FCSTD DOCUMENT  (FreeCAD 0.14R3702 (Git))
Label: Everext
License: CC-BY 3.0
LicenseURL: http://creativecommons.org/licenses/by/3.0/
objects: Mesh::Feature×51, Part::Cylinder×36, Part::Cut×32, Part::MultiFuse×20, Part::Feature×20, PartDesign::Chamfer×20, Part::FeaturePython×16, App::DocumentObjectGroup×16, Part::Box×15, PartDesign::Pad×12, Sketcher::SketchObject×9, PartDesign::Pocket×7, Part::Sweep×5, Part::Mirroring×3, PartDesign::Revolution×2, Part::Chamfer×2, Part::Helix×1
note: 221 computed .brp shape members not serialized (recipe doc carries the construction recipe); baked Part::Feature solids carry a one-line shape summary decoded from their .brp

FEATURE [PartDesign::Pad] Pad  label="Pata001"
  Length = 335
  Length2 = 100
  Placement = pos=(-110,-110,-167.5) rot=(0,0,1;0rad)
  Type = 0
FEATURE [PartDesign::Pad] Pad001  label="Pata002"
  Length = 335
  Length2 = 100
  Placement = pos=(110,-110,-167.5) rot=(0,0,1;0rad)
  Type = 0
FEATURE [PartDesign::Pad] Pad002  label="Pata003"
  Length = 335
  Length2 = 100
  Placement = pos=(-110,110,-167.5) rot=(0,0,1;0rad)
  Type = 0
FEATURE [PartDesign::Pad] Pad003  label="Pata004"
  Length = 335
  Length2 = 100
  Placement = pos=(110,110,-167.5) rot=(0,0,1;0rad)
  Type = 0
FEATURE [PartDesign::Pad] Pad004  label="Trab001"
  Length = 200
  Length2 = 100
  Placement = pos=(-100,-110,-119) rot=(0,1,0;1.5708rad)
  Type = 0
FEATURE [PartDesign::Pad] Pad005  label="Trab002"
  Length = 200
  Length2 = 100
  Placement = pos=(-110,-100,-119) rot=(0.57735,-0.57735,-0.57735;4.18879rad)
  Type = 0
FEATURE [PartDesign::Pad] Pad006  label="Trab003"
  Length = 200
  Length2 = 100
  Placement = pos=(110,-100,-119) rot=(0.57735,-0.57735,-0.57735;4.18879rad)
  Type = 0
FEATURE [PartDesign::Pad] Pad007  label="Trab004"
  Length = 200
  Length2 = 100
  Placement = pos=(-100,110,-119) rot=(0,1,0;1.5708rad)
  Type = 0
FEATURE [PartDesign::Pad] Pad008  label="Trab005"
  Length = 200
  Length2 = 100
  Placement = pos=(-100,-110,157.5) rot=(0,1,0;1.5708rad)
  Type = 0
FEATURE [PartDesign::Pad] Pad009  label="Trab006"
  Length = 200
  Length2 = 100
  Placement = pos=(-110,-100,157.5) rot=(0.57735,-0.57735,-0.57735;4.18879rad)
  Type = 0
FEATURE [PartDesign::Pad] Pad010  label="Trab007"
  Length = 200
  Length2 = 100
  Placement = pos=(110,-100,157.5) rot=(0.57735,-0.57735,-0.57735;4.18879rad)
  Type = 0
FEATURE [PartDesign::Pad] Pad011  label="Trab008"
  Length = 200
  Length2 = 100
  Placement = pos=(-100,110,157.5) rot=(0,1,0;1.5708rad)
  Type = 0
FEATURE [PartDesign::Pocket] Pocket006
  Length = 3
  Type = 0
FEATURE [Part::FeaturePython] refine  label="motor"  # WARN: FeaturePython — macro-defined, semantics opaque (R4)
  Base = -> Pocket006
  Placement = pos=(68,100,60.5) rot=(0,0,1;0rad)
FEATURE [Part::Cylinder] Cylinder008  label="BarraIz"
  Angle = 360
  Height = 190
  Placement = pos=(-110,-99,117.5) rot=(-0.57735,0.57735,0.57735;2.0944rad)
  Radius = 4
FEATURE [Part::FeaturePython] refine001  label="motor001"  # WARN: FeaturePython — macro-defined, semantics opaque (R4)
  Base = -> Pocket006
  Placement = pos=(-68,100,60.5) rot=(0,0,1;0rad)
FEATURE [Part::Cylinder] Cylinder009  label="barraM8Xmotor"
  Angle = 360
  Height = 190
  Placement = pos=(95,-12,105.5) rot=(0.707107,0,-0.707107;3.14159rad)
  Radius = 4
FEATURE [Part::Cylinder] Cylinder010  label="BarraDer"
  Angle = 360
  Height = 190
  Placement = pos=(110,-99,117.5) rot=(-0.57735,0.57735,0.57735;2.0944rad)
  Radius = 4
FEATURE [App::DocumentObjectGroup] Grupo006  label="barras"
  Group = -> [Cylinder008,Cylinder010]
FEATURE [Part::Cylinder] Cylinder011  label="barraM8X"
  Angle = 360
  Height = 190
  Placement = pos=(95,-12,129.5) rot=(0.707107,0,-0.707107;3.14159rad)
  Radius = 4
FEATURE [Part::Cylinder] Cylinder014  label="barraM8008"
  Angle = 360
  Height = 235
  Placement = pos=(-35,79,-116.5) rot=(0,0,1;0rad)
  Radius = 4
FEATURE [Part::Cylinder] Cylinder015  label="barraM8009"
  Angle = 360
  Height = 235
  Placement = pos=(35,79,-116.5) rot=(0,0,1;0rad)
  Radius = 4
FEATURE [Mesh::Feature] Z_lift
  Placement = pos=(107,253.5,219.1) rot=(0,0,1;1.5708rad)
FEATURE [Mesh::Feature] printable_lm8uu_v007  label="printable-lm8uu-v004"
  Placement = pos=(33.4,85.2,-3.9) rot=(0,0,1;0rad)
FEATURE [Mesh::Feature] printable_lm8uu_v008  label="printable-lm8uu-v005"
  Placement = pos=(-36.6,85.2,-3.9) rot=(0,0,1;0rad)
FEATURE [Part::Box] Box  label="tablelisa"
  Height = 3
  Length = 120
  Placement = pos=(53,45,161) rot=(0,0,1;0rad)
  Width = 120
FEATURE [Part::FeaturePython] refine002  label="motor002"  # WARN: FeaturePython — macro-defined, semantics opaque (R4)
  Placement = pos=(0,79,-168) rot=(0,0,1;0rad)
FEATURE [Part::Cylinder] Cylinder016  label="Cilindro008"
  Angle = 360
  Height = 10
  Placement = pos=(79.5,114.1,158) rot=(0,0,1;0rad)
  Radius = 2.6
FEATURE [Part::Cylinder] Cylinder017  label="Cilindro009"
  Angle = 360
  Height = 10
  Placement = pos=(144.5,114.1,158) rot=(0,0,1;0rad)
  Radius = 2.6
FEATURE [Part::Cylinder] Cylinder018  label="Cilindro010"
  Angle = 360
  Height = 10
  Placement = pos=(144.5,152.1,158) rot=(0,0,1;0rad)
  Radius = 2.6
FEATURE [Part::Cylinder] Cylinder019  label="Cilindro011"
  Angle = 360
  Height = 10
  Placement = pos=(79.5,152.1,158) rot=(0,0,1;0rad)
  Radius = 2.6
FEATURE [Part::Cut] Cut008
  Base = -> Box
  Tool = -> Cylinder016
FEATURE [Part::Cut] Cut009
  Base = -> Cut008
  Tool = -> Cylinder017
FEATURE [Part::Cut] Cut010
  Base = -> Cut009
  Tool = -> Cylinder019
FEATURE [Part::Cut] Cut011  label="mesainf01"
  Base = -> Cut010
  Tool = -> Cylinder018
FEATURE [Part::Box] Box001  label="tablelisa001"
  Height = 3
  Length = 120
  Placement = pos=(53,45,174) rot=(0,0,1;0rad)
  Width = 120
FEATURE [Sketcher::SketchObject] Sketch
  Placement = pos=(53,45,177) rot=(0,0,1;0rad)
  Support = -> Box001 [Face6]
  sketch-geometry (3):
    g0: Circle CenterX=5 CenterY=5 CenterZ=0 NormalX=0 NormalY=0 NormalZ=1 Radius=1.5
    g1: Circle CenterX=115 CenterY=5 CenterZ=0 NormalX=0 NormalY=0 NormalZ=1 Radius=1.5
    g2: Circle CenterX=60 CenterY=105 CenterZ=0 NormalX=0 NormalY=0 NormalZ=1 Radius=1.5
  constraints (9):
    c: Equal(g2,g1)
    c: Equal(g1,g0)
    c: Radius(g0) = 1.5
    c: DistanceY(g-1,g0) = 5
    c: DistanceX(g-1,g0) = 5
    c: DistanceY(g-1,g1) = 5
    c: DistanceX(g-1,g1) = 115
    c: DistanceY(g-1,g2) = 105
    c: DistanceX(g-1,g2) = 60
FEATURE [PartDesign::Pocket] Pocket  label="mesasup"
  Length = 5
  Placement = pos=(53,45,174) rot=(0,0,1;0rad)
  Sketch = -> Sketch
  Type = 1
FEATURE [Sketcher::SketchObject] Sketch001
  ExternalGeometry = -> [Cut011]
  Placement = pos=(0,0,164) rot=(0,0,1;0rad)
  Support = -> Cut011 [Face3]
  sketch-geometry (3):
    g0: Circle CenterX=58 CenterY=50 CenterZ=0 NormalX=0 NormalY=0 NormalZ=1 Radius=1.5
    g1: Circle CenterX=168 CenterY=50 CenterZ=0 NormalX=0 NormalY=0 NormalZ=1 Radius=1.5
    g2: Circle CenterX=113 CenterY=150 CenterZ=0 NormalX=0 NormalY=0 NormalZ=1 Radius=1.5
  constraints (9):
    c: Equal(g2,g1)
    c: Equal(g1,g0)
    c: Radius(g1) = 1.5
    c: DistanceX(g0,g-4) = -5
    c: DistanceY(g0,g-4) = -5
    c: DistanceX(g1,g-4) = 5
    c: DistanceY(g1,g-4) = -5
    c: DistanceX(g2,g-3) = -60
    c: DistanceY(g2,g-3) = 15
FEATURE [PartDesign::Pocket] Pocket007  label="mesainf"
  Length = 5
  Sketch = -> Sketch001
  Type = 1
FEATURE [Part::MultiFuse] Fusion004
FEATURE [Part::Helix] Helix  label="Muelletrazo"
  Angle = 0
  Height = 9.4
  LocalCoord = 0
  Pitch = 1
  Placement = pos=(0,0,8) rot=(0,0,1;0rad)
  Radius = 2.5
  Style = 1
FEATURE [Part::Sweep] Sweep
  Frenet = true
  Solid = true
  Spine = -> Helix [Edge1]
  Transition = 1
FEATURE [Part::MultiFuse] Fusion005  label="tonillocama"
  Placement = pos=(-54,-59,-11) rot=(0,0,1;0rad)
  Shapes = -> [Fusion004,Sweep]
FEATURE [Part::Sweep] Sweep001
  Frenet = true
  Solid = true
  Spine = -> Helix [Edge1]
  Transition = 1
FEATURE [Part::MultiFuse] Fusion006
FEATURE [Part::MultiFuse] Fusion007  label="tonillocama001"
  Placement = pos=(56,-59,-11) rot=(0,0,1;0rad)
  Shapes = -> [Fusion006,Sweep001]
FEATURE [Part::Cut] Cut012
FEATURE [Part::FeaturePython] Array  # Draft array (typed FeaturePython)
  Angle = 360
  ArrayType = 1
  Axis = (0,0,1)
  Center = (0,0,0)
  IntervalX = (1,0,0)
  IntervalY = (0,1,0)
  IntervalZ = (0,0,1)
  NumberPolar = 12
  NumberX = 2
  NumberY = 2
  NumberZ = 1
FEATURE [Part::Cut] Cut013
  Base = -> Cut012
  Placement = pos=(-54,-59,-10.3) rot=(0,0,1;0rad)
  Tool = -> Array
FEATURE [Part::Cut] Cut014
FEATURE [Part::FeaturePython] Array001  # Draft array (typed FeaturePython)
  Angle = 360
  ArrayType = 1
  Axis = (0,0,1)
  Center = (0,0,0)
  IntervalX = (1,0,0)
  IntervalY = (0,1,0)
  IntervalZ = (0,0,1)
  NumberPolar = 12
  NumberX = 2
  NumberY = 2
  NumberZ = 1
FEATURE [Part::Cut] Cut015
  Base = -> Cut014
  Placement = pos=(56,-59,-10.3) rot=(0,0,1;0rad)
  Tool = -> Array001
FEATURE [Part::Box] Box002  label="metraquilato"
  Height = 4
  Length = 104
  Placement = pos=(-51,-56,9.8) rot=(0,0,1;0rad)
  Width = 104
FEATURE [Part::Cylinder] Cylinder029  label="Cilindro021"
  Angle = 360
  Height = 40
  Radius = 8
FEATURE [Part::Cylinder] Cylinder030  label="Cilindro022"
  Angle = 360
  Height = 4.6
  Radius = 8
FEATURE [Part::Cylinder] Cylinder031  label="Cilindro023"
  Angle = 360
  Height = 10
  Placement = pos=(0,0,-2) rot=(0,0,1;0rad)
  Radius = 6
FEATURE [Part::Cut] Cut018
  Base = -> Cylinder030
  Placement = pos=(0,0,30.6) rot=(0,0,1;0rad)
  Tool = -> Cylinder031
FEATURE [Part::Cut] Cut019
  Base = -> Cylinder029
  Tool = -> Cut018
FEATURE [Part::Cylinder] Cylinder032  label="Cilindro024"
  Angle = 360
  Height = 42
  Placement = pos=(0,0,-1) rot=(0,0,1;0rad)
  Radius = 3.25
FEATURE [Part::Cut] Cut020
  Base = -> Cut019
  Tool = -> Cylinder032
FEATURE [Part::Cylinder] Cylinder033  label="Cilindro025"
  Angle = 360
  Height = 4.2
  Placement = pos=(0,0,-1) rot=(0,0,1;0rad)
  Radius = 4
FEATURE [Sketcher::SketchObject] Sketch005
  Placement = pos=(0,0,0) rot=(1,0,0;1.5708rad)
  sketch-geometry (4):
    g0: LineSegment [constr] StartX=-5 StartY=0 StartZ=0 EndX=5 EndY=0 EndZ=0
    g1: LineSegment StartX=-11.6906 StartY=3.86281 StartZ=0 EndX=-1.29847 EndY=-2.13708 EndZ=0
    g2: LineSegment StartX=-11.6906 StartY=-2.13708 StartZ=0 EndX=-11.6906 EndY=3.86281 EndZ=0
    g3: LineSegment StartX=-11.6906 StartY=-2.13708 StartZ=0 EndX=-1.29847 EndY=-2.13708 EndZ=0
  constraints (11):
    c: PointOnObject(g0,g-1)
    c: PointOnObject(g0,g-1)
    c: DistanceX(g0,g0) = -10
    c: Coincident(g2,g1)
    c: Vertical(g2)
    c: PointOnObject(g0,g1)
    c: Symmetric(g0,g0,g-2)
    c: Coincident(g3,g2)
    c: Coincident(g3,g1)
    c: Horizontal(g3)
    c: Angle(g0,g1) = 2.61799
FEATURE [Part::Cut] Cut021
  Base = -> Cut020
  Tool = -> Cylinder033
FEATURE [PartDesign::Revolution] Revolution
  Angle = 360
  Axis = (0,0,1)
  Base = (0,0,0)
  Placement = pos=(0,0,0) rot=(1,0,0;1.5708rad)
  ReferenceAxis = -> Sketch005 [V_Axis]
  Sketch = -> Sketch005
FEATURE [Part::Cut] Cut022
  Base = -> Cut021
  Tool = -> Revolution
FEATURE [Part::Cylinder] Cylinder034  label="Cilindro026"
  Angle = 360
  Height = 10
  Placement = pos=(4.2,0,0) rot=(0,1,0;1.5708rad)
  Radius = 1
FEATURE [Part::Cylinder] Cylinder035  label="Cilindro027"
  Angle = 360
  Height = 2
  Placement = pos=(0,0,-1) rot=(0,0,1;0rad)
  Radius = 4.2
FEATURE [Part::Cylinder] Cylinder036  label="Cilindro028"
  Angle = 60
  Height = 2
  Placement = pos=(0,0,-1) rot=(0,0,1;0rad)
  Radius = 14.2
FEATURE [Part::Cut] Cut023
  Base = -> Cylinder036
  Tool = -> Cylinder035
FEATURE [Part::Cylinder] Cylinder037  label="Cilindro029"
  Angle = 360
  Height = 10
  Placement = pos=(2.1,3.63731,0) rot=(-0.447214,0.774597,0.447214;1.82348rad)
  Radius = 1
FEATURE [Part::MultiFuse] Fusion010
  Shapes = -> [Cylinder034,Cut023]
FEATURE [Part::MultiFuse] Fusion011
  Shapes = -> [Cylinder037,Fusion010]
FEATURE [Part::FeaturePython] Array003  # Draft array (typed FeaturePython)
  Angle = 360
  ArrayType = 1
  Axis = (0,0,1)
  Base = -> Fusion011
  Center = (0,0,0)
  IntervalX = (1,0,0)
  IntervalY = (0,1,0)
  IntervalZ = (0,0,1)
  NumberPolar = 4
  NumberX = 1
  NumberY = 1
  NumberZ = 1
  Placement = pos=(0,0,13.5) rot=(0,0,1;0.261799rad)
FEATURE [Part::MultiFuse] Fusion012
  Shapes = -> [Cylinder037,Fusion010]
FEATURE [Part::FeaturePython] Array004  # Draft array (typed FeaturePython)
  Angle = 360
  ArrayType = 1
  Axis = (0,0,1)
  Base = -> Fusion012
  Center = (0,0,0)
  IntervalX = (1,0,0)
  IntervalY = (0,1,0)
  IntervalZ = (0,0,1)
  NumberPolar = 4
  NumberX = 1
  NumberY = 1
  NumberZ = 1
  Placement = pos=(0,0,16.5) rot=(0,0,1;0.261799rad)
FEATURE [Part::FeaturePython] Array005  # Draft array (typed FeaturePython)
  Angle = 360
  ArrayType = 1
  Axis = (0,0,1)
  Base = -> Fusion011
  Center = (0,0,0)
  IntervalX = (1,0,0)
  IntervalY = (0,1,0)
  IntervalZ = (0,0,1)
  NumberPolar = 4
  NumberX = 1
  NumberY = 1
  NumberZ = 1
  Placement = pos=(0,0,22.5) rot=(0,0,1;0.261799rad)
FEATURE [Part::MultiFuse] Fusion013
  Shapes = -> [Cylinder037,Fusion010]
FEATURE [Part::FeaturePython] Array006  # Draft array (typed FeaturePython)
  Angle = 360
  ArrayType = 1
  Axis = (0,0,1)
  Base = -> Fusion013
  Center = (0,0,0)
  IntervalX = (1,0,0)
  IntervalY = (0,1,0)
  IntervalZ = (0,0,1)
  NumberPolar = 4
  NumberX = 1
  NumberY = 1
  NumberZ = 1
  Placement = pos=(0,0,19.5) rot=(0,0,1;0.261799rad)
FEATURE [Part::MultiFuse] Fusion014
  Shapes = -> [Cylinder037,Fusion010]
FEATURE [Part::FeaturePython] Array007  # Draft array (typed FeaturePython)
  Angle = 360
  ArrayType = 1
  Axis = (0,0,1)
  Base = -> Fusion014
  Center = (0,0,0)
  IntervalX = (1,0,0)
  IntervalY = (0,1,0)
  IntervalZ = (0,0,1)
  NumberPolar = 4
  NumberX = 1
  NumberY = 1
  NumberZ = 1
  Placement = pos=(0,0,25.5) rot=(0,0,1;0.261799rad)
FEATURE [Part::Box] Box003  label="Cubo"
  Height = 8
  Length = 3
  Placement = pos=(6.5,-10,0) rot=(0,0,1;0rad)
  Width = 20
FEATURE [Part::Box] Box004  label="Cubo001"
  Height = 8
  Length = 3
  Placement = pos=(-9.5,-10,0) rot=(0,0,1;0rad)
  Width = 20
FEATURE [Part::Cut] Cut024
  Base = -> Cut022
  Tool = -> Box003
FEATURE [Part::Cut] Cut025
  Base = -> Cut024
  Tool = -> Box004
FEATURE [Part::Cut] Cut026
  Base = -> Cut025
  Tool = -> Array003
FEATURE [Part::Cut] Cut027
  Base = -> Cut026
  Tool = -> Array004
FEATURE [Part::Cut] Cut028
  Base = -> Cut027
  Tool = -> Array007
FEATURE [Part::Cut] Cut029
  Base = -> Cut028
  Tool = -> Array006
FEATURE [Part::Cut] Cut030
  Base = -> Cut029
  Tool = -> Array005
FEATURE [Part::Cylinder] Cylinder038  label="Cilindro030"
  Angle = 360
  Height = 2
  Placement = pos=(-1,5.2,16.5) rot=(0,1,0;1.5708rad)
  Radius = 1
FEATURE [Part::FeaturePython] Array008  # Draft array (typed FeaturePython)
  Angle = 360
  ArrayType = 1
  Axis = (0,0,1)
  Base = -> Cylinder038
  Center = (0,0,0)
  IntervalX = (1,0,0)
  IntervalY = (0,1,0)
  IntervalZ = (0,0,1)
  NumberPolar = 4
  NumberX = 0
  NumberY = 0
  NumberZ = 0
FEATURE [Part::Cylinder] Cylinder039  label="Cilindro031"
  Angle = 360
  Height = 2
  Placement = pos=(-1,5.2,16.5) rot=(0,1,0;1.5708rad)
  Radius = 1
FEATURE [Part::FeaturePython] Array009  # Draft array (typed FeaturePython)
  Angle = 360
  ArrayType = 1
  Axis = (0,0,1)
  Base = -> Cylinder039
  Center = (0,0,0)
  IntervalX = (1,0,0)
  IntervalY = (0,1,0)
  IntervalZ = (0,0,1)
  NumberPolar = 4
  NumberX = 0
  NumberY = 0
  NumberZ = 0
  Placement = pos=(0,0,3) rot=(0,0,1;0rad)
FEATURE [Part::Cylinder] Cylinder040  label="Cilindro032"
  Angle = 360
  Height = 2
  Placement = pos=(-1,5.2,16.5) rot=(0,1,0;1.5708rad)
  Radius = 1
FEATURE [Part::FeaturePython] Array010  # Draft array (typed FeaturePython)
  Angle = 360
  ArrayType = 1
  Axis = (0,0,1)
  Base = -> Cylinder040
  Center = (0,0,0)
  IntervalX = (1,0,0)
  IntervalY = (0,1,0)
  IntervalZ = (0,0,1)
  NumberPolar = 4
  NumberX = 0
  NumberY = 0
  NumberZ = 0
  Placement = pos=(0,0,6) rot=(0,0,1;0rad)
FEATURE [Part::Cylinder] Cylinder041  label="Cilindro033"
  Angle = 360
  Height = 2
  Placement = pos=(-1,5.2,16.5) rot=(0,1,0;1.5708rad)
  Radius = 1
FEATURE [Part::FeaturePython] Array011  # Draft array (typed FeaturePython)
  Angle = 360
  ArrayType = 1
  Axis = (0,0,1)
  Base = -> Cylinder041
  Center = (0,0,0)
  IntervalX = (1,0,0)
  IntervalY = (0,1,0)
  IntervalZ = (0,0,1)
  NumberPolar = 4
  NumberX = 0
  NumberY = 0
  NumberZ = 0
  Placement = pos=(0,0,9) rot=(0,0,1;0rad)
FEATURE [Part::Cut] Cut031
  Base = -> Cut030
  Tool = -> Array008
FEATURE [Part::Cut] Cut032
  Base = -> Cut031
  Tool = -> Array009
FEATURE [Part::Cut] Cut033
  Base = -> Cut032
  Tool = -> Array010
FEATURE [Part::Cut] Cut034  label="cuerpo j-head"
  Base = -> Cut033
  Placement = pos=(-2,13,76) rot=(0,0,-1;1.5708rad)
  Tool = -> Array011
FEATURE [Sketcher::SketchObject] Sketch006
  Placement = pos=(12.7,0,0) rot=(0.57735,0.57735,0.57735;2.0944rad)
  sketch-geometry (1):
    g0: Circle CenterX=12.1 CenterY=4.1 CenterZ=0 NormalX=0 NormalY=0 NormalZ=1 Radius=3
  constraints (1):
    c: Radius(g0) = 3
FEATURE [PartDesign::Pocket] Pocket010
  Length = 5
  Sketch = -> Sketch006
  Type = 1
FEATURE [PartDesign::Revolution] Revolution001
  Angle = 360
  Axis = (0,0,1)
  Base = (0,0,0)
  Placement = pos=(6.35,5,0) rot=(1,0,0;1.5708rad)
FEATURE [Part::MultiFuse] Fusion015  label="hotend"
  Placement = pos=(-7,19.5,67) rot=(0,0,-1;1.5708rad)
  Shapes = -> [Pocket010,Revolution001]
FEATURE [App::DocumentObjectGroup] Grupo014  label="J-Head"
  Group = -> [Fusion015,Cut034]
FEATURE [Part::Feature] Pocket007001  label="mesainf002"
  Placement = pos=(0,-5,0.2) rot=(0,0,1;0rad)
  shape: bbox 120 x 120 x 3 mm, 13 faces (baked)
FEATURE [Part::Feature] Pocket007002  label="mesasup001"
  Placement = pos=(-112,-109,-167.3) rot=(0,0,1;0rad)
  shape: bbox 120 x 120 x 3 mm, 9 faces (baked)
FEATURE [Sketcher::SketchObject] Sketch007
  Placement = pos=(0,-5,161.2) rot=(1,0,0;3.14159rad)
  Support = -> Pocket007001 [Face5]
  sketch-geometry (4):
    g0: Circle CenterX=92.0359 CenterY=-98.0016 CenterZ=0 NormalX=0 NormalY=0 NormalZ=1 Radius=3
    g1: Circle CenterX=131.948 CenterY=-98.0016 CenterZ=0 NormalX=0 NormalY=0 NormalZ=1 Radius=3
    g2: Circle CenterX=92.0359 CenterY=-148.05 CenterZ=0 NormalX=0 NormalY=0 NormalZ=1 Radius=3
    g3: Circle CenterX=131.948 CenterY=-148.05 CenterZ=0 NormalX=0 NormalY=0 NormalZ=1 Radius=3
  constraints (4):
    c: Radius(g0) = 3
    c: Equal(g0,g1)
    c: Equal(g1,g3)
    c: Equal(g3,g2)
FEATURE [PartDesign::Pocket] Pocket007003  label="mesainf003"
  Length = 5
  Placement = pos=(0,-5,0.2) rot=(0,0,1;0rad)
  Sketch = -> Sketch007
  Type = 1
FEATURE [Part::Cylinder] Cylinder042  label="VarillaRoscada"
  Angle = 360
  Height = 215
  Placement = pos=(0,79,-93) rot=(0,0,1;0rad)
  Radius = 2.5
FEATURE [Part::Feature] Pocket007004  label="mesainf004"
  Placement = pos=(-112,-109,-180.3) rot=(0,0,1;0rad)
  shape: bbox 120 x 120 x 3 mm, 9 faces (baked)
FEATURE [Mesh::Feature] z_lift
  Placement = pos=(0,79,-15) rot=(0,0,-1;1.5708rad)
FEATURE [Mesh::Feature] z_lower_bracket
  Placement = pos=(0,79,-111) rot=(0,0,1;1.5708rad)
FEATURE [Mesh::Feature] coupler
  Placement = pos=(0,79,-105) rot=(0,0,1;0rad)
FEATURE [Mesh::Feature] z_upper_bracket
  Placement = pos=(0,79,113.5) rot=(0,0,1;1.5708rad)
FEATURE [Part::Box] Box005  label="TablaBase"
  Height = 5
  Length = 204
  Placement = pos=(-102,-102,-121) rot=(0,0,1;0rad)
  Width = 204
FEATURE [Part::Sweep] Sweep002
  Frenet = true
  Solid = true
  Spine = -> Helix [Edge1]
  Transition = 1
FEATURE [Part::MultiFuse] Fusion016
FEATURE [Part::FeaturePython] Array012  # Draft array (typed FeaturePython)
  Angle = 360
  ArrayType = 1
  Axis = (0,0,1)
  Center = (0,0,0)
  IntervalX = (1,0,0)
  IntervalY = (0,1,0)
  IntervalZ = (0,0,1)
  NumberPolar = 12
  NumberX = 2
  NumberY = 2
  NumberZ = 1
FEATURE [Part::Cut] Cut035
FEATURE [Part::Cut] Cut
  Base = -> Cut035
  Placement = pos=(-54,51,-10.3) rot=(0,0,1;0rad)
  Tool = -> Array012
FEATURE [Part::MultiFuse] Fusion017
FEATURE [Part::MultiFuse] Fusion018  label="tonillocama002"
  Placement = pos=(56,51,-11) rot=(0,0,1;0rad)
  Shapes = -> [Fusion016,Sweep002]
FEATURE [Part::FeaturePython] Array013  # Draft array (typed FeaturePython)
  Angle = 360
  ArrayType = 1
  Axis = (0,0,1)
  Center = (0,0,0)
  IntervalX = (1,0,0)
  IntervalY = (0,1,0)
  IntervalZ = (0,0,1)
  NumberPolar = 12
  NumberX = 2
  NumberY = 2
  NumberZ = 1
FEATURE [Part::Sweep] Sweep003
  Frenet = true
  Solid = true
  Spine = -> Helix [Edge1]
  Transition = 1
FEATURE [Part::MultiFuse] Fusion019  label="tonillocama003"
  Placement = pos=(-54,51,-11) rot=(0,0,1;0rad)
  Shapes = -> [Fusion017,Sweep003]
FEATURE [Part::Cut] Cut037
FEATURE [Part::Cut] Cut036
  Base = -> Cut037
  Placement = pos=(56,51,-10.3) rot=(0,0,1;0rad)
  Tool = -> Array013
FEATURE [Part::Box] Box006  label="Cubo003"
  Height = 3
  Length = 102
  Placement = pos=(-50,48,9.7) rot=(0,0,1;0rad)
  Width = 8
FEATURE [Part::Box] Box007  label="Cubo004"
  Height = 3
  Length = 8
  Placement = pos=(53,-55,9.7) rot=(0,0,1;0rad)
  Width = 102
FEATURE [Part::Box] Box008  label="Cubo005"
  Height = 3
  Length = 8
  Placement = pos=(-59,-55,9.7) rot=(0,0,1;0rad)
  Width = 102
FEATURE [Part::Box] Box009  label="Cubo006"
  Height = 3
  Length = 62
  Placement = pos=(-30,-64,9.7) rot=(0,0,1;0rad)
  Width = 8
FEATURE [App::DocumentObjectGroup] Grupo015  label="Mesa"
  Group = -> [Cut,Fusion018,Cut036,Fusion019,Fusion005,Fusion007,Cut013,Cut015,Pocket007004,Pocket007002,Box002,Box006,Box007,Box008,Box009]
FEATURE [Part::Cylinder] Cylinder  label="Cilindro"
  Angle = 360
  Height = 60
  Placement = pos=(15,84,63) rot=(0,0,1;0rad)
  Radius = 2.5
FEATURE [Mesh::Feature] knob_endstop_z
  Placement = pos=(15,84,119) rot=(0,0,1;0rad)
FEATURE [Mesh::Feature] knob_endstop_z001
  Placement = pos=(15,84,62) rot=(0,0,1;0rad)
FEATURE [Part::Cylinder] Cylinder043  label="Cilindro034"
  Angle = 360
  Height = 5
  Radius = 8
FEATURE [Part::Cylinder] Cylinder044  label="Cilindro035"
  Angle = 360
  Height = 5
  Radius = 6.5
FEATURE [Part::Cylinder] Cylinder045  label="Cilindro036"
  Angle = 360
  Height = 4.5
  Placement = pos=(0,0,0.25) rot=(0,0,1;0rad)
  Radius = 6.5
FEATURE [Part::Cylinder] Cylinder046  label="Cilindro037"
  Angle = 360
  Height = 5
  Radius = 4
FEATURE [Part::Cylinder] Cylinder047  label="Cilindro038"
  Angle = 360
  Height = 5
  Radius = 2.5
FEATURE [Part::Cut] Cut038
  Base = -> Cylinder043
  Tool = -> Cylinder044
FEATURE [Part::Chamfer] Chamfer
  Base = -> Cylinder046
  Edges = 2 edges r=0.25: [Edge1,Edge3]
FEATURE [Part::Chamfer] Chamfer008
  Base = -> Cut038
  Edges = 4 edges r=0.25: [Edge1,Edge3,Edge4,Edge5]
FEATURE [Part::MultiFuse] Fusion
  Shapes = -> [Chamfer008,Cylinder045]
FEATURE [Part::MultiFuse] Fusion020
  Shapes = -> [Fusion,Chamfer]
FEATURE [Part::Cut] Cut039  label="Rodamiento625"
  Base = -> Fusion020
  Placement = pos=(0,79,114) rot=(0,0,1;0rad)
  Tool = -> Cylinder047
FEATURE [Mesh::Feature] corner
  Placement = pos=(100,-100,-79) rot=(0,1,0;1.5708rad)
FEATURE [Mesh::Feature] corner001
  Placement = pos=(-120,-100,-79) rot=(0,1,0;1.5708rad)
FEATURE [Mesh::Feature] corner002
  Placement = pos=(120,100,-79) rot=(0.707107,0,-0.707107;3.14159rad)
FEATURE [Mesh::Feature] corner003
  Placement = pos=(-100,100,-79) rot=(0.707107,0,-0.707107;3.14159rad)
FEATURE [Mesh::Feature] corner004
  Placement = pos=(70,120,-109) rot=(1,0,0;1.5708rad)
FEATURE [Mesh::Feature] corner005
  Placement = pos=(70,-100,-109) rot=(1,0,0;1.5708rad)
FEATURE [Mesh::Feature] corner006
  Placement = pos=(-70,-120,-109) rot=(0,0.707107,0.707107;3.14159rad)
FEATURE [Mesh::Feature] corner007
  Placement = pos=(-70,100,-109) rot=(0,0.707107,0.707107;3.14159rad)
FEATURE [Part::Box] Box010  label="TablaTras"
  Height = 335
  Length = 240
  Placement = pos=(-120,120,-167.5) rot=(0,0,1;0rad)
  Width = 4
FEATURE [Part::Feature] Cut040
  shape: bbox 12 x 34 x 48 mm, 1168 faces, 0 solids (baked)
FEATURE [Part::Mirroring] Part__Mirroring  label="Cut001 (Mirror #1)"
  Base = (12,0,0)
  Normal = (1,0,0)
  Source = -> Cut040
FEATURE [Part::MultiFuse] Fusion021  label="CarroX"
  Placement = pos=(-19,0,93.5) rot=(0,0,-1;1.5708rad)
  Shapes = -> [Cut040,Part__Mirroring]
FEATURE [Mesh::Feature] printable_lm8uu_v009  label="printable-lm8uu007"
  Placement = pos=(-2.7,-10.4,111.7) rot=(0.57735,-0.57735,-0.57735;2.0944rad)
FEATURE [Part::Feature] belt_holder
  Placement = pos=(15,-19,113.5) rot=(0,0,-1;1.5708rad)
  shape: bbox 34 x 2.38 x 12.24 mm, 447 faces, 0 solids (baked)
FEATURE [Part::Feature] belt_holder001  label="belt_holder005"
  Placement = pos=(24,15,28) rot=(0,1,0;3.14159rad)
  shape: bbox 3.47 x 17 x 12.24 mm, 87 faces, 0 solids (baked)
FEATURE [Mesh::Feature] printable_lm8uu_v010  label="printable-lm8uu002"
  Placement = pos=(-2.7,-10.4,135.7) rot=(0.57735,-0.57735,-0.57735;2.0944rad)
FEATURE [Part::Mirroring] Part__Mirroring001  label="belt_holder005 (Mirror #2)"
  Base = (0,17,0)
  Normal = (0,1,0)
  Source = -> belt_holder001
FEATURE [Part::MultiFuse] Fusion022  label="belt_holder2"
  Placement = pos=(-19,0,93.5) rot=(0,0,-1;1.5708rad)
  Shapes = -> [Part__Mirroring001,belt_holder001]
FEATURE [Part::Feature] Cut041  label="Polea"
  Placement = pos=(-68,100,112.5) rot=(0,0,1;0rad)
  shape: bbox 18 x 18 x 14.6 mm, 50 faces (baked)
FEATURE [PartDesign::Chamfer] Chamfer009  label="rodamiento003"
  Placement = pos=(-91,-96,113.5) rot=(-1,0,0;1.5708rad)
  Size = 0.2
FEATURE [Mesh::Feature] top_pulley_GT  label="top_pulley_GT006"
  Placement = pos=(-91,-96,142.5) rot=(1,0,0;3.14159rad)
FEATURE [PartDesign::Chamfer] Chamfer010  label="rodamiento002"
  Placement = pos=(-91,-96,117.5) rot=(-1,0,0;1.5708rad)
  Size = 0.2
FEATURE [Mesh::Feature] idler_hbot_R
  Placement = pos=(-120,-90,147.5) rot=(1,0,0;3.14159rad)
FEATURE [Mesh::Feature] idler_hbot_L
  Placement = pos=(-120,-90,127.5) rot=(1,0,0;3.14159rad)
FEATURE [PartDesign::Chamfer] Chamfer011  label="rodamiento001"
  Placement = pos=(91,-96,121.5) rot=(0,0.707107,0.707107;3.14159rad)
  Size = 0.2
FEATURE [Mesh::Feature] top_pulley_GT001  label="top_pulley_GT2"
  Placement = pos=(91,-96,122.5) rot=(0,0,1;3.14159rad)
FEATURE [PartDesign::Chamfer] Chamfer012  label="rodamiento"
  Placement = pos=(91,-96,117.5) rot=(0,0.707107,0.707107;3.14159rad)
  Size = 0.2
FEATURE [Mesh::Feature] idler_hbot_R001
  Placement = pos=(120,-90,107.5) rot=(0,0,1;3.14159rad)
FEATURE [Mesh::Feature] idler_hbot_L001
  Placement = pos=(120,-90,127.5) rot=(0,0,1;3.14159rad)
FEATURE [App::DocumentObjectGroup] Grupo018  label="HbotFrenteDerecha"
  Group = -> [idler_hbot_L001,idler_hbot_R001,Chamfer012,top_pulley_GT001,Chamfer011]
FEATURE [Mesh::Feature] top_pulley_GT002  label="top_pulley_GT007"
  Placement = pos=(-91,94,122.5) rot=(0,0,1;0rad)
FEATURE [PartDesign::Chamfer] Chamfer013  label="rodamiento005"
  Placement = pos=(-83.5,84.5,117.5) rot=(-1,0,0;1.5708rad)
  Size = 0.2
FEATURE [Mesh::Feature] top_pulley_GT003  label="top_pulley_GT008"
  Placement = pos=(-83.5,84.5,122.5) rot=(0,0,1;0rad)
FEATURE [PartDesign::Chamfer] Chamfer014  label="rodamiento004"
  Placement = pos=(-91,94,117.5) rot=(-1,0,0;1.5708rad)
  Size = 0.2
FEATURE [PartDesign::Chamfer] Chamfer015  label="rodamiento006"
  Placement = pos=(-91,94,113.5) rot=(-1,0,0;1.5708rad)
  Size = 0.2
FEATURE [PartDesign::Chamfer] Chamfer016  label="rodamiento007"
  Placement = pos=(-83.5,84.5,113.5) rot=(-1,0,0;1.5708rad)
  Size = 0.2
FEATURE [Mesh::Feature] motor_R
  Placement = pos=(-120,75,127.5) rot=(0,0,1;0rad)
FEATURE [Mesh::Feature] motor_L
  Placement = pos=(-120,75,107.5) rot=(0,0,1;0rad)
FEATURE [App::DocumentObjectGroup] Grupo019  label="MotorIzquierda"
  Group = -> [motor_L,motor_R,Chamfer016,Chamfer015,Chamfer014,Chamfer013,top_pulley_GT002,top_pulley_GT003,refine001,Cut041]
FEATURE [Mesh::Feature] top_pulley_GT004  label="top_pulley_GT009"
  Placement = pos=(91,94,142.5) rot=(0,1,0;3.14159rad)
FEATURE [PartDesign::Chamfer] Chamfer017  label="rodamiento008"
  Placement = pos=(83.5,84.5,117.5) rot=(0,0.707107,0.707107;3.14159rad)
  Size = 0.2
FEATURE [Mesh::Feature] top_pulley_GT005  label="top_pulley_GT010"
  Placement = pos=(83.5,84.5,142.5) rot=(0,1,0;3.14159rad)
FEATURE [PartDesign::Chamfer] Chamfer018  label="rodamiento009"
  Placement = pos=(91,94,117.5) rot=(0,0.707107,0.707107;3.14159rad)
  Size = 0.2
FEATURE [PartDesign::Chamfer] Chamfer019  label="rodamiento010"
  Placement = pos=(91,94,121.5) rot=(0,0.707107,0.707107;3.14159rad)
  Size = 0.2
FEATURE [PartDesign::Chamfer] Chamfer020  label="rodamiento011"
  Placement = pos=(83.5,84.5,121.5) rot=(0,0.707107,0.707107;3.14159rad)
  Size = 0.2
FEATURE [Mesh::Feature] motor_R001
  Placement = pos=(120,75,127.5) rot=(0,1,0;3.14159rad)
FEATURE [Mesh::Feature] motor_L001
  Placement = pos=(120,75,147.5) rot=(0,1,0;3.14159rad)
FEATURE [Part::Feature] Cut042  label="Polea001"
  Placement = pos=(68,100,112.5) rot=(0,0,1;0rad)
  shape: bbox 18 x 18 x 14.6 mm, 50 faces (baked)
FEATURE [App::DocumentObjectGroup] Grupo020  label="MotorDerecha"
  Group = -> [motor_L001,motor_R001,Chamfer020,Chamfer019,Chamfer018,Chamfer017,top_pulley_GT004,top_pulley_GT005,refine,Cut042]
FEATURE [Mesh::Feature] y_carriage
  Placement = pos=(-120,-43,99.5) rot=(0,0,1;0rad)
FEATURE [Mesh::Feature] printable_lm8uu_v  label="printable-lm8uu008"
  Placement = pos=(-111.6,-25,123.7) rot=(1,0,0;1.5708rad)
FEATURE [Mesh::Feature] y_carriage001
  Placement = pos=(-120,19,135.5) rot=(1,0,0;3.14159rad)
FEATURE [PartDesign::Chamfer] Chamfer021  label="rodamiento012"
  Placement = pos=(-88,-26,117.5) rot=(1,0,0;1.5708rad)
  Size = 0.2
FEATURE [PartDesign::Chamfer] Chamfer022  label="rodamiento013"
  Placement = pos=(-88,-26,121.5) rot=(1,0,0;1.5708rad)
  Size = 0.2
FEATURE [PartDesign::Chamfer] Chamfer023  label="rodamiento014"
  Placement = pos=(-88,2,117.5) rot=(1,0,0;1.5708rad)
  Size = 0.2
FEATURE [PartDesign::Chamfer] Chamfer024  label="rodamiento015"
  Placement = pos=(-88,2,121.5) rot=(1,0,0;1.5708rad)
  Size = 0.2
FEATURE [Mesh::Feature] y_carriage002
  Placement = pos=(120,-43,135.5) rot=(0,1,0;3.14159rad)
FEATURE [Mesh::Feature] y_carriage003
  Placement = pos=(120,19,99.5) rot=(0,0,1;3.14159rad)
FEATURE [PartDesign::Chamfer] Chamfer025  label="rodamiento016"
  Placement = pos=(88,-26,117.5) rot=(0,0.707107,-0.707107;3.14159rad)
  Size = 0.2
FEATURE [PartDesign::Chamfer] Chamfer026  label="rodamiento017"
  Placement = pos=(88,-26,113.5) rot=(0,0.707107,-0.707107;3.14159rad)
  Size = 0.2
FEATURE [Mesh::Feature] printable_lm8uu_v011  label="printable-lm8uu009"
  Placement = pos=(111.6,-25,111.3) rot=(0,0.707107,-0.707107;3.14159rad)
FEATURE [PartDesign::Chamfer] Chamfer027  label="rodamiento018"
  Placement = pos=(88,2,117.5) rot=(0,0.707107,-0.707107;3.14159rad)
  Size = 0.2
FEATURE [PartDesign::Chamfer] Chamfer028  label="rodamiento019"
  Placement = pos=(88,2,113.5) rot=(0,0.707107,-0.707107;3.14159rad)
  Size = 0.2
FEATURE [Part::Cylinder] Cylinder048  label="Cilindro039"
  Angle = 360
  Height = 10
  Placement = pos=(-68,100,0) rot=(0,0,1;0rad)
  Radius = 5.5
FEATURE [Part::Cylinder] Cylinder049  label="Cilindro040"
  Angle = 360
  Height = 10
  Placement = pos=(-91,94,0) rot=(0,0,1;0rad)
  Radius = 5
FEATURE [Part::Cylinder] Cylinder050  label="Cilindro041"
  Angle = 360
  Height = 10
  Placement = pos=(-83.5,84.5,0) rot=(0,0,1;0rad)
  Radius = 5
FEATURE [Part::Cylinder] Cylinder051  label="Cilindro042"
  Angle = 360
  Height = 10
  Placement = pos=(-88,2,0) rot=(0,0,1;0rad)
  Radius = 5
FEATURE [Part::Cylinder] Cylinder052  label="Cilindro043"
  Angle = 360
  Height = 10
  Placement = pos=(-88,-26,0) rot=(0,0,1;0rad)
  Radius = 5
FEATURE [Part::Cylinder] Cylinder053  label="Cilindro044"
  Angle = 360
  Height = 10
  Placement = pos=(-91,-96,0) rot=(0,0,1;0rad)
  Radius = 5
FEATURE [Part::Box] Box011  label="Cubo007"
  Height = 2
  Length = 240
  Placement = pos=(-120,-120,4) rot=(0,0,1;0rad)
  Width = 240
FEATURE [Part::MultiFuse] Fusion023
  Shapes = -> [Cylinder048,Cylinder049,Cylinder050,Cylinder051,Cylinder052,Cylinder053]
FEATURE [Part::Mirroring] Part__Mirroring002  label="Fusion023 (Mirror #3)"
  Base = (0,0,0)
  Normal = (1,0,0)
  Source = -> Fusion023
FEATURE [Part::MultiFuse] Fusion024
  Shapes = -> [Part__Mirroring002,Fusion023]
FEATURE [Part::Cut] Cut043
  Base = -> Box011
  Placement = pos=(0,0,111.5) rot=(0,0,1;0rad)
  Tool = -> Fusion024
FEATURE [Sketcher::SketchObject] Sketch008
  ExternalGeometry = -> [Cut043]
  Placement = pos=(0,0,117.5) rot=(0,0,1;0rad)
  Support = -> Cut043 [Face3]
  sketch-geometry (25):
    g0: LineSegment StartX=-88 StartY=-3.6 StartZ=0 EndX=88 EndY=-3.6 EndZ=0
    g1: ArcOfCircle CenterX=-88 CenterY=2 CenterZ=0 NormalX=0 NormalY=0 NormalZ=1 Radius=5.6 StartAngle=3.0871 EndAngle=4.71239
    g2: ArcOfCircle CenterX=88 CenterY=2 CenterZ=0 NormalX=0 NormalY=0 NormalZ=1 Radius=5.6 StartAngle=4.71239 EndAngle=6.33768
    g3: LineSegment StartX=8.48243 StartY=-20.4 StartZ=0 EndX=88 EndY=-20.4 EndZ=0
    g4: ArcOfCircle CenterX=88 CenterY=-26 CenterZ=0 NormalX=0 NormalY=0 NormalZ=1 Radius=5.6 StartAngle=6.16547 EndAngle=7.85398
    g5: LineSegment StartX=-13.6364 StartY=-20.4 StartZ=0 EndX=-88 EndY=-20.4 EndZ=0
    g6: ArcOfCircle CenterX=-88 CenterY=-26 CenterZ=0 NormalX=0 NormalY=0 NormalZ=1 Radius=5.6 StartAngle=1.5708 EndAngle=3.2593
    g7: LineSegment StartX=-93.5612 StartY=-26.6577 StartZ=0 EndX=-85.4388 EndY=-95.3423 EndZ=0
    g8: ArcOfCircle CenterX=-91 CenterY=-96 CenterZ=0 NormalX=0 NormalY=0 NormalZ=1 Radius=5.6 StartAngle=3.14159 EndAngle=6.4009
    g9: LineSegment StartX=-96.6 StartY=-96 StartZ=0 EndX=-96.6 EndY=94 EndZ=0
    g10: LineSegment StartX=93.5612 StartY=-26.6577 StartZ=0 EndX=85.4388 EndY=-95.3423 EndZ=0
    g11: ArcOfCircle CenterX=91 CenterY=-96 CenterZ=0 NormalX=0 NormalY=0 NormalZ=1 Radius=5.6 StartAngle=3.02388 EndAngle=6.28319
    g12: LineSegment StartX=96.6 StartY=-96 StartZ=0 EndX=96.6 EndY=94 EndZ=0
    g13: LineSegment StartX=-93.5917 StartY=2.305 StartZ=0 EndX=-89.0917 EndY=84.805 EndZ=0
    g14: LineSegment StartX=93.5917 StartY=2.305 StartZ=0 EndX=89.0917 EndY=84.805 EndZ=0
    g15: ArcOfCircle CenterX=83.5 CenterY=84.5 CenterZ=0 NormalX=0 NormalY=0 NormalZ=1 Radius=5.6 StartAngle=0.0544914 EndAngle=1.34843
    g16: ArcOfCircle CenterX=91 CenterY=94 CenterZ=0 NormalX=0 NormalY=0 NormalZ=1 Radius=5.6 StartAngle=4.5961e-08 EndAngle=1.29458
    g17: LineSegment StartX=92.5272 StartY=99.3877 StartZ=0 EndX=69.6636 EndY=105.869 EndZ=0
    g18: LineSegment StartX=84.735 StartY=89.9621 StartZ=0 EndX=66.6547 EndY=94.0502 EndZ=0
    g19: ArcOfCircle CenterX=68 CenterY=100 CenterZ=0 NormalX=0 NormalY=0 NormalZ=1 Radius=6.1 StartAngle=1.29458 EndAngle=4.49002
    g20: LineSegment StartX=-92.5272 StartY=99.3877 StartZ=0 EndX=-69.6636 EndY=105.869 EndZ=0
    g21: LineSegment StartX=-84.735 StartY=89.9621 StartZ=0 EndX=-66.6547 EndY=94.0502 EndZ=0
    g22: ArcOfCircle CenterX=-68 CenterY=100 CenterZ=0 NormalX=0 NormalY=0 NormalZ=1 Radius=6.1 StartAngle=4.93476 EndAngle=8.1302
    g23: ArcOfCircle CenterX=-91 CenterY=94 CenterZ=0 NormalX=0 NormalY=0 NormalZ=1 Radius=5.6 StartAngle=1.84702 EndAngle=3.14159
    g24: ArcOfCircle CenterX=-83.5 CenterY=84.5 CenterZ=0 NormalX=0 NormalY=0 NormalZ=1 Radius=5.6 StartAngle=1.79316 EndAngle=3.08711
  constraints (74):
    c: Horizontal(g0)
    c: Coincident(g1,g-4)
    c: Coincident(g1,g0)
    c: Coincident(g2,g-12)
    c: Coincident(g2,g0)
    c: Horizontal(g3)
    c: Coincident(g4,g-13)
    c: Coincident(g4,g3)
    c: Horizontal(g5)
    c: Coincident(g6,g-5)
    c: Coincident(g6,g5)
    c: Coincident(g7,g6)
    c: Coincident(g8,g-3)
    c: Coincident(g8,g7)
    c: Coincident(g9,g8)
    c: Coincident(g10,g4)
    c: Coincident(g11,g-14)
    c: Coincident(g11,g10)
    c: Coincident(g12,g11)
    c: Coincident(g13,g1)
    c: Coincident(g14,g2)
    c: Radius(g11) = 5.6
    c: Tangent(g10,g11)
    c: Tangent(g12,g11)
    c: Radius(g8) = 5.6
    c: Tangent(g7,g8)
    c: Tangent(g8,g9)
    c: Radius(g6) = 5.6
    c: Tangent(g6,g7)
    c: Tangent(g5,g6)
    c: Radius(g1) = 5.6
    c: Tangent(g13,g1)
    c: Tangent(g0,g1)
    c: Radius(g2) = 5.6
    c: Tangent(g14,g2)
    c: Radius(g4) = 5.6
    c: Tangent(g3,g4)
    c: Tangent(g10,g4)
    c: Coincident(g15,g-11)
    c: Coincident(g15,g14)
    c: Radius(g15) = 5.6
    c: Tangent(g15,g14)
    c: Coincident(g16,g-10)
    c: Coincident(g16,g12)
    c: Radius(g16) = 5.6
    c: Tangent(g16,g12)
    c: Coincident(g19,g-9)
    c: Coincident(g19,g17)
    c: Coincident(g19,g18)
    c: Radius(g19) = 6.1
    c: Tangent(g19,g18)
    c: Tangent(g19,g17)
    c: Coincident(g17,g16)
    c: Coincident(g18,g15)
    c: Tangent(g15,g18)
    c: Tangent(g17,g16)
    c: Coincident(g22,g-6)
    c: Coincident(g22,g21)
    c: Radius(g22) = 6.1
    c: Coincident(g22,g20)
    c: Tangent(g20,g22)
    c: Tangent(g22,g21)
    c: Coincident(g23,g-8)
    c: Coincident(g23,g20)
    c: Coincident(g23,g9)
    c: Coincident(g24,g-7)
    c: Coincident(g24,g21)
    c: Coincident(g24,g13)
    c: Radius(g24) = 5.6
    c: Radius(g23) = 5.6
    c: Tangent(g21,g24)
    c: Tangent(g23,g20)
    c: Tangent(g23,g9)
    c: Tangent(g13,g24)
FEATURE [Part::Box] Box012  label="Cubo008"
  Height = 10
  Length = 2
  Placement = pos=(-16,-23,113) rot=(0,0,1;0rad)
  Width = 5
FEATURE [Sketcher::SketchObject] Sketch009
  Placement = pos=(-14,-23,113) rot=(0.57735,0.57735,0.57735;2.0944rad)
  Support = -> Box012 [Face2]
  sketch-geometry (4):
    g0: LineSegment StartX=2.0622 StartY=8.14173 StartZ=0 EndX=3.2622 EndY=8.14173 EndZ=0
    g1: LineSegment StartX=3.2622 StartY=8.14173 StartZ=0 EndX=3.2622 EndY=1.14173 EndZ=0
    g2: LineSegment StartX=3.2622 StartY=1.14173 StartZ=0 EndX=2.0622 EndY=1.14173 EndZ=0
    g3: LineSegment StartX=2.0622 StartY=1.14173 StartZ=0 EndX=2.0622 EndY=8.14173 EndZ=0
  constraints (10):
    c: Coincident(g0,g1)
    c: Coincident(g1,g2)
    c: Coincident(g2,g3)
    c: Coincident(g3,g0)
    c: Horizontal(g0)
    c: Horizontal(g2)
    c: Vertical(g1)
    c: Vertical(g3)
    c: DistanceX(g2) = -1.2
    c: DistanceY(g1) = -7
FEATURE [Part::Sweep] Sweep004  label="Correa"
  Frenet = true
  Sections = -> [Sketch009]
  Solid = true
  Spine = -> Sketch008 [Edge21]
  Transition = 1
FEATURE [Mesh::Feature] corner008
  Placement = pos=(70,-100,147.5) rot=(0,0,1;0rad)
FEATURE [Mesh::Feature] corner009
  Placement = pos=(100,70,147.5) rot=(0,0,1;1.5708rad)
FEATURE [Mesh::Feature] corner010
  Placement = pos=(-70,100,147.5) rot=(0,0,1;3.14159rad)
FEATURE [Mesh::Feature] corner011
  Placement = pos=(-100,-70,147.5) rot=(0,0,-1;1.5708rad)
FEATURE [Mesh::Feature] corner012
  Placement = pos=(120,70,107.5) rot=(0.57735,0.57735,-0.57735;4.18879rad)
FEATURE [Mesh::Feature] corner013
  Placement = pos=(-100,70,107.5) rot=(0.57735,0.57735,-0.57735;4.18879rad)
FEATURE [Mesh::Feature] corner014
  Placement = pos=(70,-120,107.5) rot=(-1,0,0;1.5708rad)
FEATURE [Mesh::Feature] corner015
  Placement = pos=(-70,-100,107.5) rot=(0,0.707107,-0.707107;3.14159rad)
FEATURE [App::DocumentObjectGroup] Grupo016  label="Anclajes"
  Group = -> [corner,corner001,corner002,corner003,corner004,corner005,corner006,corner007,corner008,corner009,corner010,corner011,corner012,corner013,corner014,corner015]
FEATURE [Mesh::Feature] endstop_x
  Placement = pos=(-96,-29.5,135.5) rot=(0,0,1;0rad)
FEATURE [Mesh::Feature] endstop_y
  Placement = pos=(-120,-100,107.5) rot=(-1,0,0;1.5708rad)
FEATURE [Part::Box] Box013  label="TablaTras001"
  Height = 335
  Length = 240
  Placement = pos=(-120,-124,-167.5) rot=(0,0,1;0rad)
  Width = 4
FEATURE [Sketcher::SketchObject] Sketch010
  ExternalGeometry = -> [Box013]
  Placement = pos=(-120,-124,-167.5) rot=(1,0,0;1.5708rad)
  Support = -> Box013 [Face3]
  sketch-geometry (14):
    g0: LineSegment StartX=40 StartY=95 StartZ=0 EndX=200 EndY=95 EndZ=0
    g1: LineSegment StartX=220 StartY=115 StartZ=0 EndX=220 EndY=275 EndZ=0
    g2: LineSegment StartX=200 StartY=295 StartZ=0 EndX=40 EndY=295 EndZ=0
    g3: LineSegment StartX=20 StartY=275 StartZ=0 EndX=20 EndY=115 EndZ=0
    g4: LineSegment StartX=45 StartY=0 StartZ=0 EndX=195 EndY=0 EndZ=0
    g5: LineSegment StartX=195 StartY=0 StartZ=0 EndX=195 EndY=20 EndZ=0
    g6: LineSegment StartX=175 StartY=40 StartZ=0 EndX=65 EndY=40 EndZ=0
    g7: LineSegment StartX=45 StartY=20 StartZ=0 EndX=45 EndY=0 EndZ=0
    g8: ArcOfCircle CenterX=40 CenterY=275 CenterZ=0 NormalX=0 NormalY=0 NormalZ=1 Radius=20 StartAngle=1.5708 EndAngle=3.14159
    g9: ArcOfCircle CenterX=40 CenterY=115 CenterZ=0 NormalX=0 NormalY=0 NormalZ=1 Radius=20 StartAngle=3.14159 EndAngle=4.71239
    g10: ArcOfCircle CenterX=200 CenterY=115 CenterZ=0 NormalX=0 NormalY=0 NormalZ=1 Radius=20 StartAngle=4.71239 EndAngle=6.28319
    g11: ArcOfCircle CenterX=200 CenterY=275 CenterZ=0 NormalX=0 NormalY=0 NormalZ=1 Radius=20 StartAngle=0 EndAngle=1.5708
    g12: ArcOfCircle CenterX=175 CenterY=20 CenterZ=0 NormalX=0 NormalY=0 NormalZ=1 Radius=20 StartAngle=0 EndAngle=1.5708
    g13: ArcOfCircle CenterX=65 CenterY=20 CenterZ=0 NormalX=0 NormalY=0 NormalZ=1 Radius=20 StartAngle=1.5708 EndAngle=3.14159
  constraints (36):
    c: Horizontal(g0)
    c: Horizontal(g2)
    c: Vertical(g1)
    c: Vertical(g3)
    c: Coincident(g4,g5)
    c: Coincident(g7,g4)
    c: Horizontal(g4)
    c: Horizontal(g6)
    c: Vertical(g5)
    c: Vertical(g7)
    c: PointOnObject(g4,g-1)
    c: Tangent(g2,g8)
    c: Tangent(g3,g8)
    c: Tangent(g3,g9)
    c: Tangent(g0,g9)
    c: Tangent(g0,g10)
    c: Tangent(g1,g10)
    c: Tangent(g2,g11)
    c: Tangent(g1,g11)
    c: Tangent(g6,g12)
    c: Tangent(g5,g12)
    c: Tangent(g6,g13)
    c: Tangent(g7,g13)
    c: Equal(g9,g8)
    c: Equal(g8,g11)
    c: Equal(g11,g10)
    c: Equal(g10,g12)
    c: Equal(g12,g13)
    c: Radius(g10) = 20
    c: DistanceX(g4) = 150
    c: DistanceX(g3,g1) = 200
    c: DistanceY(g2,g0) = -200
    c: DistanceY(g6,g4) = -40
    c: DistanceX(g-1,g3) = 20
    c: DistanceY(g2,g-3) = 40
    c: DistanceX(g-1,g4) = 45
FEATURE [PartDesign::Pocket] Pocket007005  label="PanelDel"
  Length = 5
  Placement = pos=(-120,-124,-167.5) rot=(0,0,1;0rad)
  Sketch = -> Sketch010
  Type = 1
FEATURE [Part::Box] Box014  label="TablaTras002"
  Height = 335
  Length = 4
  Placement = pos=(-124,-124,-167.5) rot=(0,0,1;0rad)
  Width = 248
FEATURE [Sketcher::SketchObject] Sketch011
  ExternalGeometry = -> [Box014]
  Placement = pos=(-124,-124,-167.5) rot=(0.57735,-0.57735,-0.57735;2.0944rad)
  Support = -> Box014 [Face1]
  sketch-geometry (8):
    g0: LineSegment StartX=-183 StartY=295 StartZ=0 EndX=-73 EndY=295 EndZ=0
    g1: LineSegment StartX=-53 StartY=275 StartZ=0 EndX=-53 EndY=165 EndZ=0
    g2: LineSegment StartX=-73 StartY=145 StartZ=0 EndX=-183 EndY=145 EndZ=0
    g3: LineSegment StartX=-203 StartY=165 StartZ=0 EndX=-203 EndY=275 EndZ=0
    g4: ArcOfCircle CenterX=-73 CenterY=275 CenterZ=0 NormalX=0 NormalY=0 NormalZ=1 Radius=20 StartAngle=0 EndAngle=1.5708
    g5: ArcOfCircle CenterX=-73 CenterY=165 CenterZ=0 NormalX=0 NormalY=0 NormalZ=1 Radius=20 StartAngle=4.71239 EndAngle=6.28319
    g6: ArcOfCircle CenterX=-183 CenterY=165 CenterZ=0 NormalX=0 NormalY=0 NormalZ=1 Radius=20 StartAngle=3.14159 EndAngle=4.71239
    g7: ArcOfCircle CenterX=-183 CenterY=275 CenterZ=0 NormalX=0 NormalY=0 NormalZ=1 Radius=20 StartAngle=1.5708 EndAngle=3.14159
  constraints (20):
    c: Horizontal(g0)
    c: Horizontal(g2)
    c: Vertical(g1)
    c: Vertical(g3)
    c: Tangent(g0,g4)
    c: Tangent(g1,g4)
    c: Tangent(g2,g5)
    c: Tangent(g1,g5)
    c: Tangent(g3,g6)
    c: Tangent(g2,g6)
    c: Tangent(g0,g7)
    c: Tangent(g3,g7)
    c: Equal(g7,g4)
    c: Equal(g4,g5)
    c: Equal(g5,g6)
    c: Radius(g4) = 20
    c: DistanceY(g2,g0) = 150
    c: DistanceX(g1,g3) = -150
    c: DistanceX(g3,g-3) = -45
    c: DistanceY(g0,g-3) = 40
FEATURE [PartDesign::Pocket] Pocket007006
  Length = 5
  Placement = pos=(-124,-124,-167.5) rot=(0,0,1;0rad)
  Sketch = -> Sketch011
  Type = 1
FEATURE [App::DocumentObjectGroup] Grupo013  label="ocultar"
  Group = -> [Box,Z_lift,Box001,Cut011,Helix,Pocket,Pocket007,Pocket007001,Pocket007003,Cut043,Sketch008,Box012,Box013,Box014,Pocket007006]
FEATURE [Part::Feature] Pocket007007  label="LateralIz"
  shape: bbox 4 x 248 x 335 mm, 14 faces (baked)
FEATURE [Part::Feature] Pocket007008  label="LateralDer"
  Placement = pos=(244,0,0) rot=(0,0,1;0rad)
  shape: bbox 4 x 248 x 335 mm, 14 faces (baked)
FEATURE [App::DocumentObjectGroup] Grupo  label="T-Slot"
  Group = -> [Pad006,Pad007,Pad008,Pad009,Pad010,Pad011,Pad005,Pad,Pad001,Pad002,Pad003,Pad004,Box005,Box010,Pocket007005,Pocket007007,Pocket007008]
FEATURE [Part::Feature] Part__Feature  label="Inferior"
  Placement = pos=(-81,-12,141) rot=(0,0,1;0rad)
  shape: bbox 10.5 x 20 x 6.5 mm, 37 faces (baked)
FEATURE [Part::Feature] Part__Feature001  label="Superior"
  Placement = pos=(-81,-12,141) rot=(0,0,1;0rad)
  shape: bbox 14 x 20 x 6.5 mm, 19 faces (baked)
FEATURE [Part::Feature] Part__Feature002  label="Pestaña"
  Placement = pos=(-81,-12,141) rot=(0,0,1;0rad)
  shape: bbox 8.605 x 20.99 x 4 mm, 10 faces (baked)
FEATURE [Part::Feature] Part__Feature003  label="Inferior001"
  Placement = pos=(-110,-76,95) rot=(-0.57735,-0.57735,0.57735;2.0944rad)
  shape: bbox 6.5 x 10.5 x 20 mm, 37 faces (baked)
FEATURE [Part::Feature] Part__Feature004  label="Superior001"
  Placement = pos=(-110,-76,95) rot=(-0.57735,-0.57735,0.57735;2.0944rad)
  shape: bbox 6.5 x 14 x 20 mm, 19 faces (baked)
FEATURE [Part::Feature] Part__Feature005  label="Pesta?a001"
  Placement = pos=(-110,-76,95) rot=(-0.57735,-0.57735,0.57735;2.0944rad)
  shape: bbox 4 x 8.605 x 20.99 mm, 10 faces (baked)
FEATURE [App::DocumentObjectGroup] Grupo017  label="HbotFrenteIzquierda"
  Group = -> [idler_hbot_L,idler_hbot_R,Chamfer010,top_pulley_GT,Chamfer009,endstop_y,Part__Feature003,Part__Feature004,Part__Feature005]
FEATURE [Part::Feature] Part__Feature006  label="Inferior002"
  Placement = pos=(15,84.5,8) rot=(-0.57735,-0.57735,-0.57735;2.0944rad)
  shape: bbox 20 x 6.5 x 10.5 mm, 37 faces (baked)
FEATURE [Part::Feature] Part__Feature007  label="Superior002"
  Placement = pos=(15,84.5,8) rot=(-0.57735,-0.57735,-0.57735;2.0944rad)
  shape: bbox 20 x 6.5 x 14 mm, 19 faces (baked)
FEATURE [Part::Feature] Part__Feature008  label="Pesta?a002"
  Placement = pos=(15,84.5,8) rot=(-0.57735,-0.57735,-0.57735;2.0944rad)
  shape: bbox 20.99 x 4 x 8.605 mm, 10 faces (baked)
FEATURE [App::DocumentObjectGroup] Grupo011  label="EjeZ"
  Group = -> [Cylinder014,Cylinder015,printable_lm8uu_v007,printable_lm8uu_v008,Cylinder042,z_lift,z_lower_bracket,coupler,z_upper_bracket,Grupo015,Cylinder,knob_endstop_z,knob_endstop_z001,Cut039,refine002,Part__Feature006,Part__Feature007,Part__Feature008]
FEATURE [Part::Feature] Cut044  label="hotend-holder"
  Placement = pos=(0,0,-17) rot=(0,0,1;0rad)
  shape: bbox 34 x 43 x 59.1 mm, 663 faces (baked)
FEATURE [App::DocumentObjectGroup] Grupo009  label="carro"
  Group = -> [Fusion022,belt_holder,printable_lm8uu_v010,printable_lm8uu_v009,Fusion021,Cylinder009,Cylinder011,Cut044]
FEATURE [Mesh::Feature] printable_lm8uu_v012  label="printable-lm8uu010"
  Placement = pos=(-111.6,0,123.7) rot=(1,0,0;1.5708rad)
FEATURE [App::DocumentObjectGroup] Grupo021  label="ExtreIzq"
  Group = -> [y_carriage,y_carriage001,Chamfer021,Chamfer022,printable_lm8uu_v,Chamfer023,Chamfer024,endstop_x,Part__Feature,Part__Feature001,Part__Feature002,printable_lm8uu_v012]
FEATURE [Mesh::Feature] printable_lm8uu_v013  label="printable-lm8uu011"
  Placement = pos=(111.6,0,111.3) rot=(0,0.707107,-0.707107;3.14159rad)
FEATURE [App::DocumentObjectGroup] Grupo022  label="ExtreDer"
  Group = -> [Chamfer025,Chamfer026,Chamfer027,y_carriage003,printable_lm8uu_v011,Chamfer028,y_carriage002,printable_lm8uu_v013]
FEATURE [App::DocumentObjectGroup] Grupo010  label="estremos"
  Group = -> [Grupo017,Grupo018,Grupo019,Grupo020,Grupo021,Grupo022]
FEATURE [App::DocumentObjectGroup] Grupo008  label="EjeXY"
  Group = -> [Grupo009,Grupo010,Grupo014,Sweep004]
